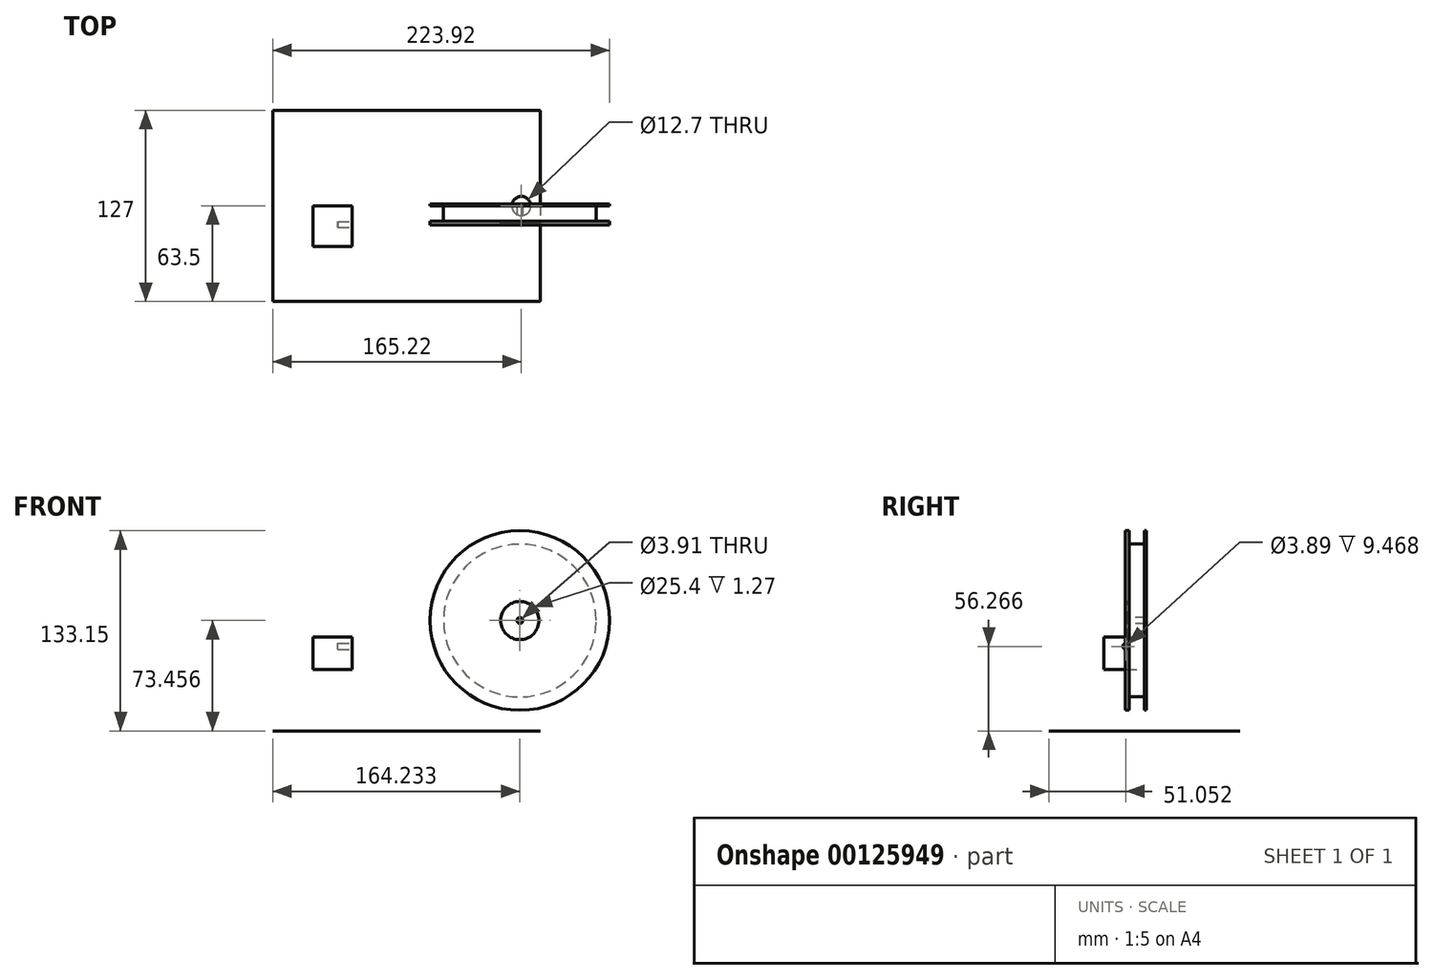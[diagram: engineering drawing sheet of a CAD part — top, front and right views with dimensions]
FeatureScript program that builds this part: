
annotation { "Feature Type Name" : "Feature", "Feature Type Description" : "" }
export const myFeature = defineFeature(function(context is Context, id is Id, definition is map)
    precondition{}
    {
        {
            var Q0;
            Q0=qCreatedBy(makeId("Top.planeOp"),FACE);
            var sketch = newSketch(context, id + "F0", { "sketchPlane" : qUnion([Q0])});
            skLineSegment(sketch, "E0.bottom", {"start": v(88.9, 63.5) * mm, "end": v(-88.9, 63.5) * mm});
            skLineSegment(sketch, "E0.top", {"start": v(88.9, -63.5) * mm, "end": v(-88.9, -63.5) * mm});
            skLineSegment(sketch, "E0.left", {"start": v(88.9, 63.5) * mm, "end": v(88.9, -63.5) * mm});
            skLineSegment(sketch, "E0.right", {"start": v(-88.9, 63.5) * mm, "end": v(-88.9, -63.5) * mm});
            skPoint(sketch, "E0.middle", {"position": v(0, 0) * mm});
            skSolve(sketch);
        }
        {
            var Q0;
            Q0 = qSketchRegion(id + "F0", true);
            extrude(context, id + "F1", {"entities" : qUnion([Q0]), "depth" : 1 / 50.8 * mm});
        }
        {
            var Q0;
            Q0=qCreatedBy(makeId("Front.planeOp"),FACE);
            var sketch = newSketch(context, id + "F2", { "sketchPlane" : qUnion([Q0])});
            skLineSegment(sketch, "E1.bottom", {"start": v(-62.26, 62.43) * mm, "end": v(-36.14, 62.43) * mm});
            skLineSegment(sketch, "E1.top", {"start": v(-62.26, 40.88) * mm, "end": v(-36.14, 40.88) * mm});
            skLineSegment(sketch, "E1.left", {"start": v(-62.26, 62.43) * mm, "end": v(-62.26, 40.88) * mm});
            skLineSegment(sketch, "E1.right", {"start": v(-36.14, 62.43) * mm, "end": v(-36.14, 40.88) * mm});
            skSolve(sketch);
        }
        {
            var Q0;
            Q0=makeQuery(id+"F2.imprint","IMPRINT",FACE,{"disambiguationData":[TD([[makeQuery(id+"F2.imprint","IMPRINT",EDGE,{"derivedFrom":sQuery(id+"F2.wireOp",EDGE,"E1.bottom")}),-1.0]])]});
            extrude(context, id + "F3", {"entities" : qUnion([Q0]), "depth" : 27.06 * mm});
        }
        {
            var Q0;
            Q0=makeQuery(id+"F3.opExtrude","SWEPT_FACE",FACE,{"disambiguationData":[OSD([sQuery(id+"F2.wireOp",EDGE,"E1.right")])]});
            var sketch = newSketch(context, id + "F4", { "sketchPlane" : qUnion([Q0])});
            skCircle(sketch, "E2", {"center": v(-12.45, 56.27) * mm, "radius": 1.94 * mm});
            skSolve(sketch);
        }
        {
            var Q0;
            Q0 = qSketchRegion(id + "F4", true);
            extrude(context, id + "F5", {"entities" : qUnion([Q0]), "operationType" : NewBodyOperationType.REMOVE, "oppositeDirection" : true, "depth" : 9.47 * mm});
        }
        {
            var Q0;
            Q0=qCreatedBy(makeId("Front.planeOp"),FACE);
            var sketch = newSketch(context, id + "F6", { "sketchPlane" : qUnion([Q0])});
            skCircle(sketch, "E3", {"center": v(75.33, 73.46) * mm, "radius": 59.7 * mm});
            skCircle(sketch, "E4", {"center": v(75.33, 73.46) * mm, "radius": 50.8 * mm});
            skSolve(sketch);
        }
        {
            var Q0;
            Q0=makeQuery(id+"F6.imprint","IMPRINT",FACE,{"disambiguationData":[TD([[makeQuery(id+"F6.imprint","IMPRINT",EDGE,{"derivedFrom":sQuery(id+"F6.wireOp",EDGE,"E4")}),1.0]])]});
            extrude(context, id + "F7", {"entities" : qUnion([Q0]), "depth" : 10.16 * mm});
        }
        {
            var Q0;
            Q0=makeQuery(id+"F6.imprint","IMPRINT",FACE,{"disambiguationData":[TD([[makeQuery(id+"F6.imprint","IMPRINT",EDGE,{"derivedFrom":sQuery(id+"F6.wireOp",EDGE,"E4")}),1.0]])]});
            var Q1;
            Q1=makeQuery(id+"F6.imprint","IMPRINT",FACE,{"disambiguationData":[TD([[makeQuery(id+"F6.imprint","IMPRINT",EDGE,{"derivedFrom":sQuery(id+"F6.wireOp",EDGE,"E3")}),1.0]])]});
            extrude(context, id + "F8", {"entities" : qUnion([Q0, Q1]), "operationType" : NewBodyOperationType.ADD, "oppositeDirection" : true, "depth" : 1.27 * mm});
        }
        {
            var Q0;
            Q0=makeQuery(id+"F7.opExtrude","CAP_FACE",FACE,{"disambiguationData":[OSD([sQuery(id+"F6.wireOp",EDGE,"E4")])],"isStart":false});
            var sketch = newSketch(context, id + "F9", { "sketchPlane" : qUnion([Q0])});
            skCircle(sketch, "E5", {"center": v(75.33, 73.46) * mm, "radius": 59.69 * mm});
            skCircle(sketch, "E6", {"center": v(75.33, 73.46) * mm, "radius": 12.7 * mm});
            skCircle(sketch, "E7", {"center": v(75.33, 73.46) * mm, "radius": 1.96 * mm});
            skSolve(sketch);
        }
        {
            var Q0;
            Q0=makeQuery(id+"F9.imprint","IMPRINT",FACE,{"disambiguationData":[TD([[makeQuery(id+"F9.imprint","IMPRINT",EDGE,{"derivedFrom":sQuery(id+"F9.wireOp",EDGE,"E7")}),1.0]])]});
            extrude(context, id + "F10", {"entities" : qUnion([Q0]), "operationType" : NewBodyOperationType.REMOVE, "oppositeDirection" : true, "depth" : 25.4 * mm, "hasSecondDirection" : true, "secondDirectionOppositeDirection" : false, "secondDirectionDepth" : 75.07 * mm});
        }
        {
            var Q0;
            Q0=makeQuery(id+"F9.imprint","IMPRINT",FACE,{"disambiguationData":[TD([[makeQuery(id+"F9.imprint","IMPRINT",EDGE,{"derivedFrom":sQuery(id+"F9.wireOp",EDGE,"E6")}),-1.0]])]});
            var Q1;
            Q1=makeQuery(id+"F9.imprint","IMPRINT",FACE,{"disambiguationData":[TD([[makeQuery(id+"F9.imprint","IMPRINT",EDGE,{"derivedFrom":sQuery(id+"F9.wireOp",EDGE,"E5")}),1.0]])]});
            extrude(context, id + "F11", {"entities" : qUnion([Q0, Q1]), "operationType" : NewBodyOperationType.ADD, "depth" : 1.27 * mm});
        }
        {
            var Q0;
            Q0=makeQuery(id+"F9.imprint","IMPRINT",FACE,{"disambiguationData":[TD([[makeQuery(id+"F9.imprint","IMPRINT",EDGE,{"derivedFrom":sQuery(id+"F9.wireOp",EDGE,"E6")}),1.0]])]});
            var Q1;
            Q1=makeQuery(id+"F11.opExtrude","CAP_FACE",FACE,{"disambiguationData":[OSD([sQuery(id+"F9.wireOp",EDGE,"E5"),sQuery(id+"F9.wireOp",EDGE,"E6")])],"isStart":false});
            extrude(context, id + "F12", {"entities" : qUnion([Q0, Q1]), "operationType" : NewBodyOperationType.ADD, "depth" : 1.27 * mm});
        }
        {
            var Q0;
            Q0=makeQuery(id+"F1.opExtrude","CAP_FACE",FACE,{"disambiguationData":[OSD([sQuery(id+"F0.wireOp",EDGE,"E0.bottom"),sQuery(id+"F0.wireOp",EDGE,"E0.top"),sQuery(id+"F0.wireOp",EDGE,"E0.left"),sQuery(id+"F0.wireOp",EDGE,"E0.right")])],"isStart":false});
            var sketch = newSketch(context, id + "F13", { "sketchPlane" : qUnion([Q0])});
            skCircle(sketch, "E8", {"center": v(76.32, 0) * mm, "radius": 6.35 * mm});
            skSolve(sketch);
        }
        {
            var Q0;
            Q0 = qSketchRegion(id + "F13", true);
            extrude(context, id + "F14", {"entities" : qUnion([Q0]), "operationType" : NewBodyOperationType.REMOVE, "oppositeDirection" : true, "depth" : 25.4 * mm});
        }
    });
